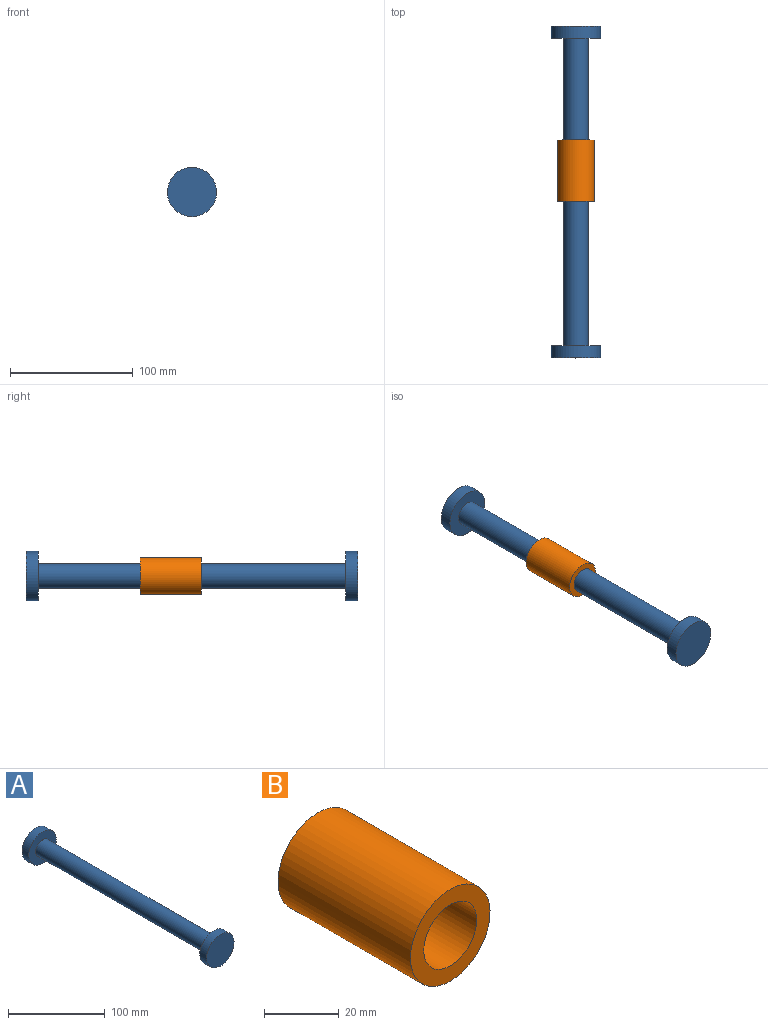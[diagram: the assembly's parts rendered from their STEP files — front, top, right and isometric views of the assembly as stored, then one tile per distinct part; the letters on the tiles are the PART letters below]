
ASSEMBLY  parts=2 mates=1
PART A: 7 faces, bbox 40x270x40 mm
  f0: cylinder r=10mm len=250mm, axis (0,-1,0), area 15708mm2, adj f1,f6
  f1: plane 40x40mm, normal (0,1,0), area 942.5mm2, adj f0,f2
  f2: cylinder r=20mm len=40mm, axis (0,-1,0), area 1256.6mm2, adj f1,f3
  f3: plane 40x40mm, normal (0,-1,0), area 1256.6mm2, adj f2
  f4: plane 40x40mm, normal (0,1,0), area 1256.6mm2, adj f5
  f5: cylinder r=20mm len=40mm, axis (0,-1,0), area 1256.6mm2, adj f4,f6
  f6: plane 40x40mm, normal (0,-1,0), area 942.5mm2, adj f0,f5
PART B: 4 faces, bbox 30x50x30 mm
  f0: cylinder r=10mm len=50mm, axis (0,1,0), area 3141.6mm2, adj f2,f3
  f1: cylinder r=15mm len=50mm, axis (0,1,0), area 4712.4mm2, adj f2,f3
  f2: plane 30x30mm, normal (0,-1,0), area 392.7mm2, adj f0,f1
  f3: plane 30x30mm, normal (0,1,0), area 392.7mm2, adj f0,f1
PLACE A t=(19.04,4.25,-41.43)mm
PLACE B t=(19.04,21.53,62.96)mm
MATE slider B.f1 <-> A.f0  axis (0,1,0) through (19.04,21.53,62.96)mm
